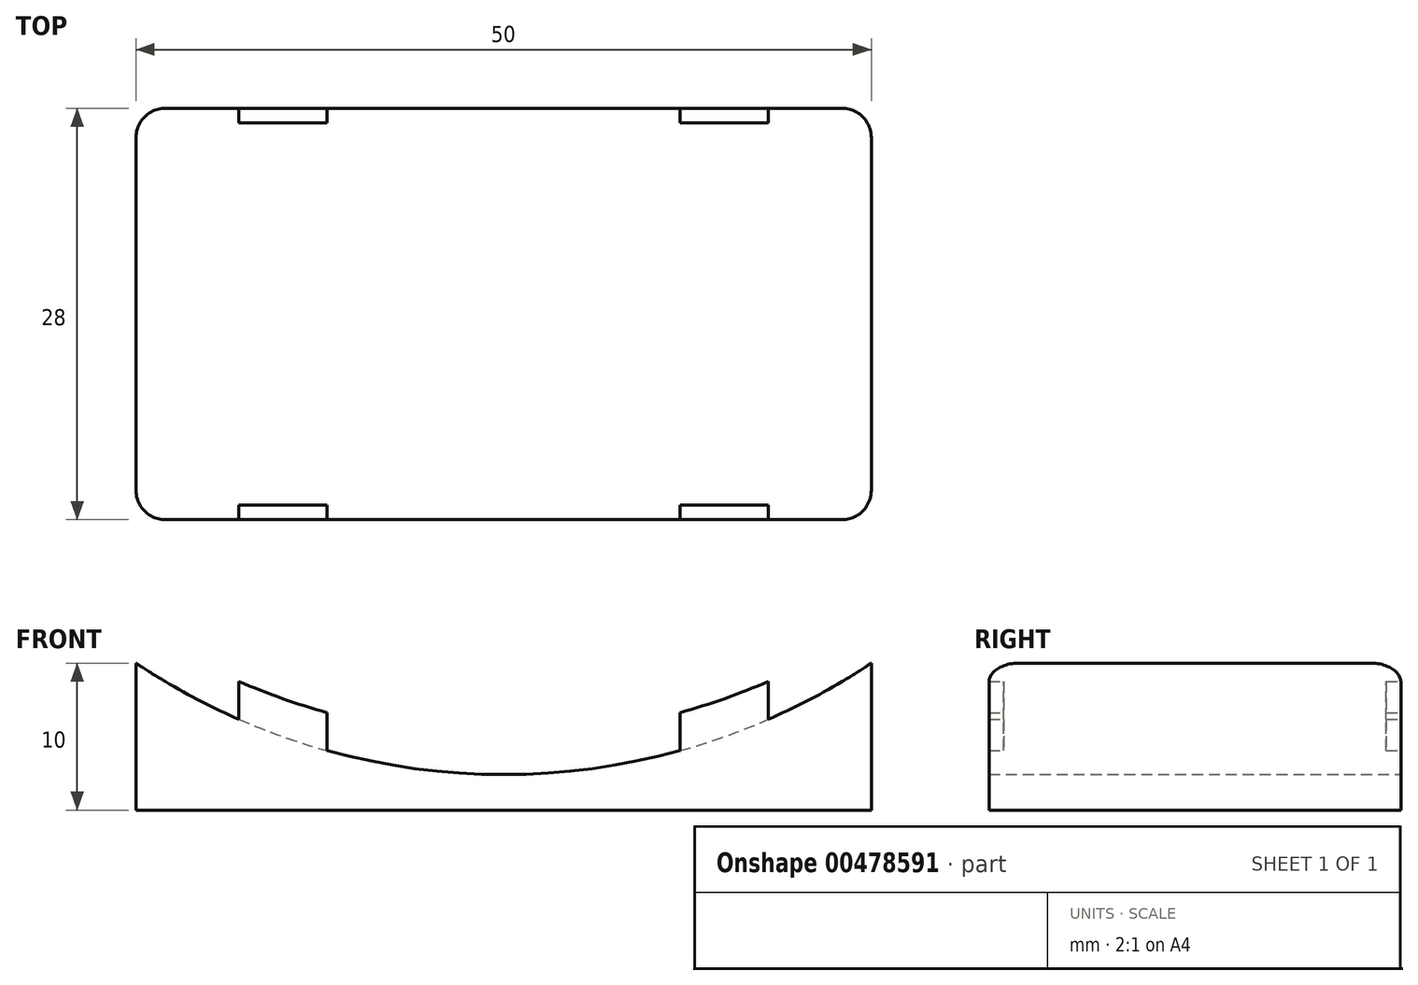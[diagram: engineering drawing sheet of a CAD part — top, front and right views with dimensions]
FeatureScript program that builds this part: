
annotation { "Feature Type Name" : "Feature", "Feature Type Description" : "" }
export const myFeature = defineFeature(function(context is Context, id is Id, definition is map)
    precondition{}
    {
        {
            var Q0;
            Q0=qCreatedBy(makeId("Front.planeOp"),FACE);
            var sketch = newSketch(context, id + "F0", { "sketchPlane" : qUnion([Q0])});
            skLineSegment(sketch, "E0.top", {"start": v(-25, 0) * mm, "end": v(25, 0) * mm});
            skLineSegment(sketch, "E0.left", {"start": v(-25, 10) * mm, "end": v(-25, 0) * mm});
            skLineSegment(sketch, "E0.right", {"start": v(25, 10) * mm, "end": v(25, 0) * mm});
            skArc(sketch, "E1", {"start": v(-25, 10) * mm, "mid": v(0, 2.42) * mm, "end": v(25, 10) * mm});
            skSolve(sketch);
        }
        {
            var Q0;
            Q0 = qSketchRegion(id + "F0", true);
            extrude(context, id + "F1", {"entities" : qUnion([Q0]), "depth" : 14 * mm, "hasSecondDirection" : true, "secondDirectionOppositeDirection" : true, "secondDirectionDepth" : 14 * mm});
        }
        {
            var Q0;
            Q0=qCreatedBy(makeId("Top.planeOp"),FACE);
            cPlane(context, id + "F2", {"entities" : qUnion([Q0]), "cplaneType" : CPlaneType.OFFSET, "offset" : 10 * mm, "width" : 150 * mm, "height" : 150 * mm});
        }
        {
            var Q0;
            Q0=qCreatedBy(id+"F2.planeOp",FACE);
            var sketch = newSketch(context, id + "F3", { "sketchPlane" : qUnion([Q0])});
            skLineSegment(sketch, "E2.0", {"start": v(-18, -14) * mm, "end": v(-12, -14) * mm});
            skLineSegment(sketch, "E3.0", {"start": v(-18, 14) * mm, "end": v(-12, 14) * mm});
            skLineSegment(sketch, "E4.top", {"start": v(-18, -13) * mm, "end": v(-12, -13) * mm});
            skLineSegment(sketch, "E4.left", {"start": v(-18, -14) * mm, "end": v(-18, -13) * mm});
            skLineSegment(sketch, "E4.right", {"start": v(-12, -14) * mm, "end": v(-12, -13) * mm});
            skLineSegment(sketch, "E5.MirrorCS", {"start": v(18, -14) * mm, "end": v(12, -14) * mm});
            skLineSegment(sketch, "E6.MirrorCS", {"start": v(18, -13) * mm, "end": v(12, -13) * mm});
            skLineSegment(sketch, "E7.MirrorCS", {"start": v(18, -14) * mm, "end": v(18, -13) * mm});
            skLineSegment(sketch, "E8.MirrorCS", {"start": v(12, -14) * mm, "end": v(12, -13) * mm});
            skLineSegment(sketch, "E9.MirrorCS", {"start": v(12, 14) * mm, "end": v(12, 13) * mm});
            skLineSegment(sketch, "E10.MirrorCS", {"start": v(18, 14) * mm, "end": v(18, 13) * mm});
            skLineSegment(sketch, "E11.MirrorCS", {"start": v(-18, 14) * mm, "end": v(-18, 13) * mm});
            skLineSegment(sketch, "E12.MirrorCS", {"start": v(-12, 14) * mm, "end": v(-12, 13) * mm});
            skLineSegment(sketch, "E13.MirrorCS", {"start": v(-18, 13) * mm, "end": v(-12, 13) * mm});
            skLineSegment(sketch, "E14.MirrorCS", {"start": v(18, 14) * mm, "end": v(12, 14) * mm});
            skLineSegment(sketch, "E15.MirrorCS", {"start": v(18, 13) * mm, "end": v(12, 13) * mm});
            skLineSegment(sketch, "E16.trimOffspring", {"start": v(12, -14) * mm, "end": v(18, -14) * mm});
            skLineSegment(sketch, "E17.trimOffspring", {"start": v(12, 14) * mm, "end": v(18, 14) * mm});
            skPoint(sketch, "E18.0.end.orphan", {"position": v(25, 14) * mm});
            skPoint(sketch, "E19.orphan", {"position": v(25, -14) * mm});
            skPoint(sketch, "E20.orphan", {"position": v(-25, -14) * mm});
            skPoint(sketch, "E21.orphan", {"position": v(-25, 14) * mm});
            skSolve(sketch);
        }
        {
            var Q0;
            Q0 = qSketchRegion(id + "F3", true);
            extrude(context, id + "F4", {"entities" : qUnion([Q0]), "operationType" : NewBodyOperationType.ADD, "oppositeDirection" : true, "depth" : 10 * mm});
        }
        {
            var Q0;
            Q0=qCreatedBy(makeId("Front.planeOp"),FACE);
            var sketch = newSketch(context, id + "F5", { "sketchPlane" : qUnion([Q0])});
            skCircle(sketch, "E22", {"center": v(0, 50) * mm, "radius": 45 * mm});
            skSolve(sketch);
        }
        {
            var Q0;
            Q0 = qSketchRegion(id + "F5", true);
            extrude(context, id + "F6", {"entities" : qUnion([Q0]), "operationType" : NewBodyOperationType.REMOVE, "depth" : 25 * mm, "hasSecondDirection" : true, "secondDirectionOppositeDirection" : true, "secondDirectionDepth" : 25 * mm});
        }
        {
            var Q0;
            Q0=makeQuery(id+"F1.opExtrude","CAP_EDGE",EDGE,{"disambiguationData":[OSD([sQuery(id+"F0.wireOp",EDGE,"E0.left")])],"isStart":true});
            var Q1;
            Q1=makeQuery(id+"F1.opExtrude","CAP_EDGE",EDGE,{"disambiguationData":[OSD([sQuery(id+"F0.wireOp",EDGE,"E0.left")])],"isStart":false});
            var Q2;
            Q2=makeQuery(id+"F1.opExtrude","CAP_EDGE",EDGE,{"disambiguationData":[OSD([sQuery(id+"F0.wireOp",EDGE,"E0.right")])],"isStart":false});
            var Q3;
            Q3=makeQuery(id+"F1.opExtrude","CAP_EDGE",EDGE,{"disambiguationData":[OSD([sQuery(id+"F0.wireOp",EDGE,"E0.right")])],"isStart":true});
            fillet(context, id + "F7", {"entities" : qUnion([Q0, Q1, Q2, Q3]), "radius" : 2 * mm, "tangentPropagation" : true, "allowEdgeOverflow" : false});
        }
    });
